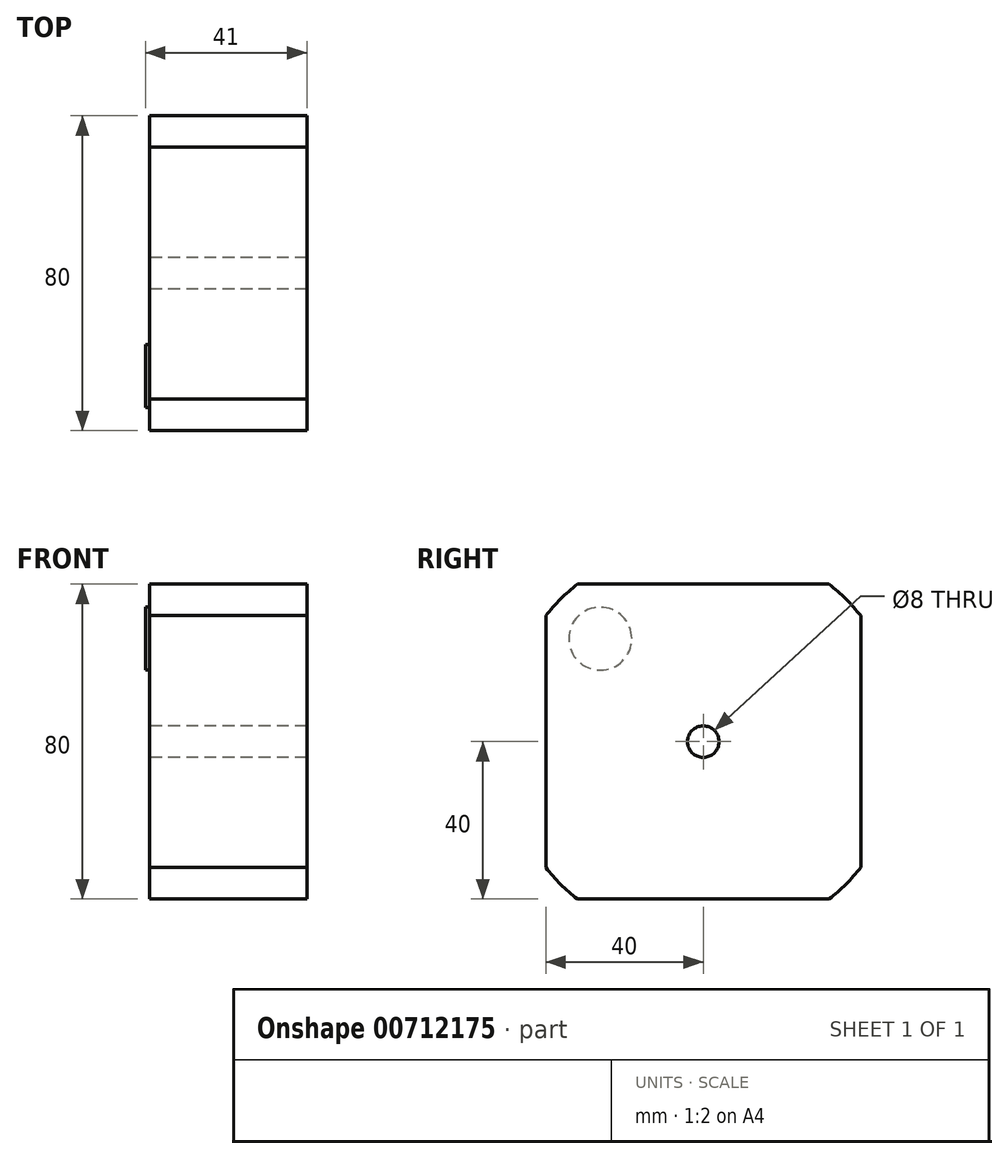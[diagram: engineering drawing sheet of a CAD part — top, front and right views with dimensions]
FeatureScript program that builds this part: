
annotation { "Feature Type Name" : "Feature", "Feature Type Description" : "" }
export const myFeature = defineFeature(function(context is Context, id is Id, definition is map)
    precondition{}
    {
        {
            var Q0;
            Q0=qCreatedBy(makeId("Right.planeOp"),FACE);
            var sketch = newSketch(context, id + "F0", { "sketchPlane" : qUnion([Q0])});
            skLineSegment(sketch, "E0.bottom", {"start": v(-40, 40) * mm, "end": v(40, 40) * mm});
            skLineSegment(sketch, "E0.top", {"start": v(-40, -40) * mm, "end": v(40, -40) * mm});
            skLineSegment(sketch, "E0.left", {"start": v(-40, 40) * mm, "end": v(-40, -40) * mm});
            skLineSegment(sketch, "E0.right", {"start": v(40, 40) * mm, "end": v(40, -40) * mm});
            skPoint(sketch, "E0.middle", {"position": v(0, 0) * mm});
            skSolve(sketch);
        }
        {
            var Q0;
            Q0 = qSketchRegion(id + "F0", true);
            extrude(context, id + "F1", {"entities" : qUnion([Q0]), "depth" : 40 * mm, "offsetDistance" : 25 * mm});
        }
        {
            var Q0;
            Q0=makeQuery(id+"F1.opExtrude","CAP_FACE",FACE,{"disambiguationData":[OSD([sQuery(id+"F0.wireOp",EDGE,"E0.bottom"),sQuery(id+"F0.wireOp",EDGE,"E0.top"),sQuery(id+"F0.wireOp",EDGE,"E0.left"),sQuery(id+"F0.wireOp",EDGE,"E0.right")])],"isStart":false});
            var sketch = newSketch(context, id + "F2", { "sketchPlane" : qUnion([Q0])});
            skArc(sketch, "E1", {"start": v(-32, 40) * mm, "mid": v(-36.22, 36.22) * mm, "end": v(-40, 32) * mm});
            skLineSegment(sketch, "E2", {"start": v(-40, 40) * mm, "end": v(-40, 32) * mm});
            skLineSegment(sketch, "E3", {"start": v(-40, 40) * mm, "end": v(-32, 40) * mm});
            skArc(sketch, "E4.1.0", {"start": v(-40, -32) * mm, "mid": v(-36.22, -36.22) * mm, "end": v(-32, -40) * mm});
            skLineSegment(sketch, "E4.1.1", {"start": v(-40, -40) * mm, "end": v(-32, -40) * mm});
            skLineSegment(sketch, "E4.1.2", {"start": v(-40, -40) * mm, "end": v(-40, -32) * mm});
            skArc(sketch, "E4.2.0", {"start": v(32, -40) * mm, "mid": v(36.22, -36.22) * mm, "end": v(40, -32) * mm});
            skLineSegment(sketch, "E4.2.1", {"start": v(40, -40) * mm, "end": v(40, -32) * mm});
            skLineSegment(sketch, "E4.2.2", {"start": v(40, -40) * mm, "end": v(32, -40) * mm});
            skArc(sketch, "E4.3.0", {"start": v(40, 32) * mm, "mid": v(36.22, 36.22) * mm, "end": v(32, 40) * mm});
            skLineSegment(sketch, "E4.3.1", {"start": v(40, 40) * mm, "end": v(32, 40) * mm});
            skLineSegment(sketch, "E4.3.2", {"start": v(40, 40) * mm, "end": v(40, 32) * mm});
            skSolve(sketch);
        }
        {
            var Q0;
            Q0 = qSketchRegion(id + "F2", true);
            extrude(context, id + "F3", {"entities" : qUnion([Q0]), "operationType" : NewBodyOperationType.REMOVE, "endBound" : BoundingType.THROUGH_ALL, "oppositeDirection" : true, "depth" : 25 * mm, "offsetDistance" : 25 * mm});
        }
        {
            var Q0;
            Q0=makeQuery(id+"F1.opExtrude","CAP_FACE",FACE,{"disambiguationData":[OSD([sQuery(id+"F0.wireOp",EDGE,"E0.bottom"),sQuery(id+"F0.wireOp",EDGE,"E0.top"),sQuery(id+"F0.wireOp",EDGE,"E0.left"),sQuery(id+"F0.wireOp",EDGE,"E0.right")])],"isStart":true});
            var sketch = newSketch(context, id + "F4", { "sketchPlane" : qUnion([Q0])});
            skCircle(sketch, "E5", {"center": v(0, 0) * mm, "radius": 4 * mm});
            skSolve(sketch);
        }
        {
            var Q0;
            Q0 = qSketchRegion(id + "F4", true);
            extrude(context, id + "F5", {"entities" : qUnion([Q0]), "operationType" : NewBodyOperationType.REMOVE, "endBound" : BoundingType.THROUGH_ALL, "oppositeDirection" : true, "depth" : 25 * mm, "offsetDistance" : 25 * mm});
        }
        {
            var Q0;
            Q0=makeQuery(id+"F1.opExtrude","CAP_FACE",FACE,{"disambiguationData":[OSD([sQuery(id+"F0.wireOp",EDGE,"E0.bottom"),sQuery(id+"F0.wireOp",EDGE,"E0.top"),sQuery(id+"F0.wireOp",EDGE,"E0.left"),sQuery(id+"F0.wireOp",EDGE,"E0.right")])],"isStart":true});
            var sketch = newSketch(context, id + "F6", { "sketchPlane" : qUnion([Q0])});
            skLineSegment(sketch, "E6", {"start": v(0, 0) * mm, "end": v(26.16, 26.16) * mm, "construction": true});
            skLineSegment(sketch, "E7", {"start": v(0, 0) * mm, "end": v(40, 0) * mm, "construction": true});
            skCircle(sketch, "E8", {"center": v(26.16, 26.16) * mm, "radius": 8 * mm});
            skCircle(sketch, "E9", {"center": v(26.16, 26.16) * mm, "radius": 13.75 * mm, "construction": true});
            skSolve(sketch);
        }
        {
            var Q0;
            Q0=makeQuery(id+"F6.imprint","IMPRINT",FACE,{"disambiguationData":[TD([[makeQuery(id+"F6.imprint","IMPRINT",EDGE,{"derivedFrom":sQuery(id+"F6.wireOp",EDGE,"E8")}),1.0]])]});
            extrude(context, id + "F7", {"entities" : qUnion([Q0]), "operationType" : NewBodyOperationType.ADD, "depth" : 1 * mm, "offsetDistance" : 25 * mm});
        }
    });
